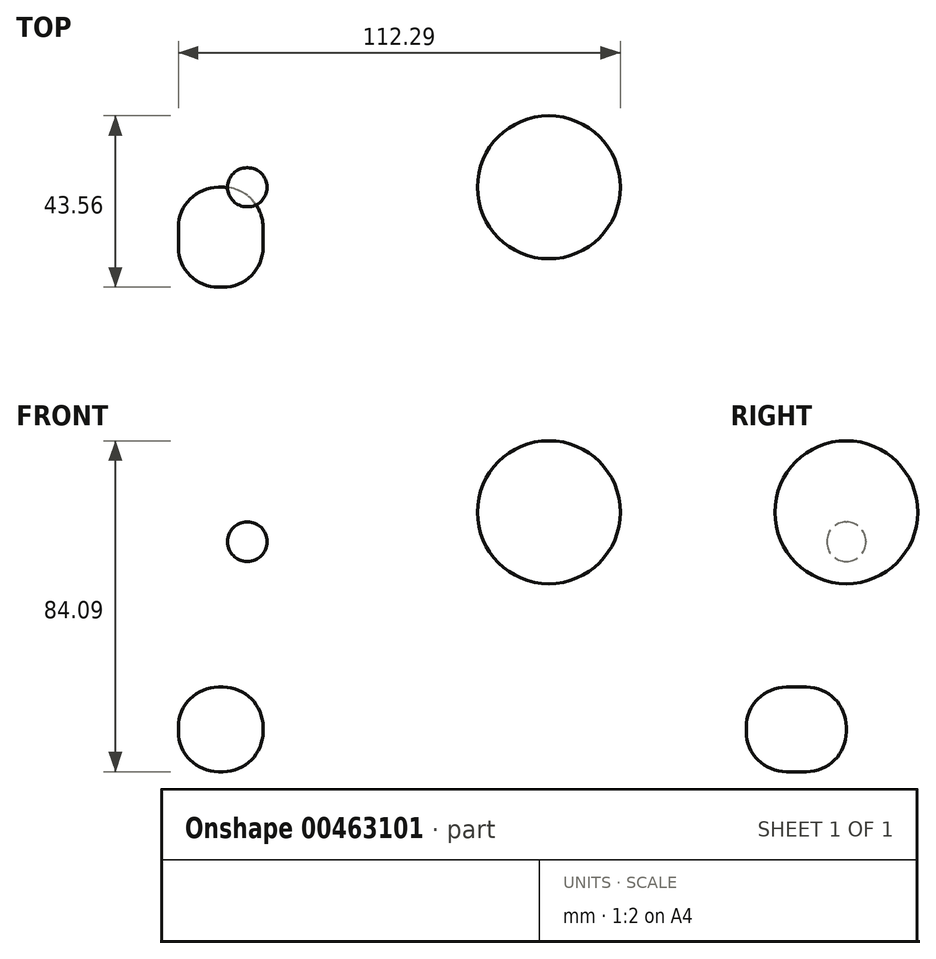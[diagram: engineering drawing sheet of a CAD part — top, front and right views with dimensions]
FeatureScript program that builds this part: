
annotation { "Feature Type Name" : "Feature", "Feature Type Description" : "" }
export const myFeature = defineFeature(function(context is Context, id is Id, definition is map)
    precondition{}
    {
        {
            var Q0;
            Q0=qCreatedBy(makeId("Top.planeOp"),FACE);
            var sketch = newSketch(context, id + "F0", { "sketchPlane" : qUnion([Q0])});
            skCircle(sketch, "E0", {"center": v(0, 0) * mm, "radius": 52.63 * mm});
            skSolve(sketch);
        }
        {
            var Q0;
            Q0=qCreatedBy(makeId("Front.planeOp"),FACE);
            var sketch = newSketch(context, id + "F1", { "sketchPlane" : qUnion([Q0])});
            skLineSegment(sketch, "E1.bottom", {"start": v(-124.76, -28.07) * mm, "end": v(-103.26, -28.07) * mm});
            skLineSegment(sketch, "E1.top", {"start": v(-124.76, -6.57) * mm, "end": v(-103.26, -6.57) * mm});
            skLineSegment(sketch, "E1.left", {"start": v(-124.76, -28.07) * mm, "end": v(-124.76, -6.57) * mm});
            skLineSegment(sketch, "E1.right", {"start": v(-103.26, -28.07) * mm, "end": v(-103.26, -6.57) * mm});
            skSolve(sketch);
        }
        {
            var Q0;
            Q0=makeQuery(id+"F1.imprint","IMPRINT",FACE,{"disambiguationData":[TD([[makeQuery(id+"F1.imprint","IMPRINT",EDGE,{"derivedFrom":sQuery(id+"F1.wireOp",EDGE,"E1.bottom")}),1.0]])]});
            extrude(context, id + "F2", {"entities" : qUnion([Q0]), "depth" : 25.4 * mm});
        }
        {
            var Q0;
            Q0=makeQuery(id+"F2.opExtrude","SWEPT_EDGE",EDGE,{"disambiguationData":[OSD([sQuery(id+"F1.wireOp",EDGE,"E1.bottom"),sQuery(id+"F1.wireOp",EDGE,"E1.right")])]});
            var Q1;
            Q1=makeQuery(id+"F2.opExtrude","CAP_EDGE",EDGE,{"disambiguationData":[OSD([sQuery(id+"F1.wireOp",EDGE,"E1.bottom")])],"isStart":false});
            var Q2;
            Q2=makeQuery(id+"F2.opExtrude","SWEPT_FACE",FACE,{"disambiguationData":[OSD([sQuery(id+"F1.wireOp",EDGE,"E1.bottom")])]});
            var Q3;
            Q3=makeQuery(id+"F2.opExtrude","CAP_FACE",FACE,{"disambiguationData":[OSD([sQuery(id+"F1.wireOp",EDGE,"E1.bottom"),sQuery(id+"F1.wireOp",EDGE,"E1.top"),sQuery(id+"F1.wireOp",EDGE,"E1.left"),sQuery(id+"F1.wireOp",EDGE,"E1.right")])],"isStart":false});
            var Q4;
            Q4=makeQuery(id+"F2.opExtrude","SWEPT_EDGE",EDGE,{"disambiguationData":[OSD([sQuery(id+"F1.wireOp",EDGE,"E1.top"),sQuery(id+"F1.wireOp",EDGE,"E1.left")])]});
            var Q5;
            Q5=makeQuery(id+"F2.opExtrude","SWEPT_FACE",FACE,{"disambiguationData":[OSD([sQuery(id+"F1.wireOp",EDGE,"E1.top")])]});
            var Q6;
            Q6=makeQuery(id+"F2.opExtrude","SWEPT_FACE",FACE,{"disambiguationData":[OSD([sQuery(id+"F1.wireOp",EDGE,"E1.left")])]});
            var Q7;
            Q7=makeQuery(id+"F2.opExtrude","CAP_EDGE",EDGE,{"disambiguationData":[OSD([sQuery(id+"F1.wireOp",EDGE,"E1.bottom")])],"isStart":true});
            var Q8;
            Q8=makeQuery(id+"F2.opExtrude","CAP_EDGE",EDGE,{"disambiguationData":[OSD([sQuery(id+"F1.wireOp",EDGE,"E1.top")])],"isStart":false});
            var Q9;
            Q9=makeQuery(id+"F2.opExtrude","CAP_FACE",FACE,{"disambiguationData":[OSD([sQuery(id+"F1.wireOp",EDGE,"E1.bottom"),sQuery(id+"F1.wireOp",EDGE,"E1.top"),sQuery(id+"F1.wireOp",EDGE,"E1.left"),sQuery(id+"F1.wireOp",EDGE,"E1.right")])],"isStart":true});
            var Q10;
            Q10=makeQuery(id+"F2.opExtrude","SWEPT_FACE",FACE,{"disambiguationData":[OSD([sQuery(id+"F1.wireOp",EDGE,"E1.right")])]});
            var Q11;
            Q11=makeQuery(id+"F2.opExtrude","SWEPT_EDGE",EDGE,{"disambiguationData":[OSD([sQuery(id+"F1.wireOp",EDGE,"E1.bottom"),sQuery(id+"F1.wireOp",EDGE,"E1.left")])]});
            var Q12;
            Q12=makeQuery(id+"F2.opExtrude","CAP_EDGE",EDGE,{"disambiguationData":[OSD([sQuery(id+"F1.wireOp",EDGE,"E1.left")])],"isStart":false});
            var Q13;
            Q13=makeQuery(id+"F2.opExtrude","CAP_EDGE",EDGE,{"disambiguationData":[OSD([sQuery(id+"F1.wireOp",EDGE,"E1.right")])],"isStart":true});
            var Q14;
            Q14=makeQuery(id+"F2.opExtrude","CAP_EDGE",EDGE,{"disambiguationData":[OSD([sQuery(id+"F1.wireOp",EDGE,"E1.left")])],"isStart":true});
            var Q15;
            Q15=makeQuery(id+"F2.opExtrude","CAP_EDGE",EDGE,{"disambiguationData":[OSD([sQuery(id+"F1.wireOp",EDGE,"E1.top")])],"isStart":true});
            var Q16;
            Q16=makeQuery(id+"F2.opExtrude","SWEPT_EDGE",EDGE,{"disambiguationData":[OSD([sQuery(id+"F1.wireOp",EDGE,"E1.top"),sQuery(id+"F1.wireOp",EDGE,"E1.right")])]});
            var Q17;
            Q17=makeQuery(id+"F2.opExtrude","CAP_EDGE",EDGE,{"disambiguationData":[OSD([sQuery(id+"F1.wireOp",EDGE,"E1.right")])],"isStart":false});
            fillet(context, id + "F3", {"entities" : qUnion([Q0, Q1, Q2, Q3, Q4, Q5, Q6, Q7, Q8, Q9, Q10, Q11, Q12, Q13, Q14, Q15, Q16, Q17]), "radius" : 10.16 * mm, "tangentPropagation" : true, "allowEdgeOverflow" : false});
        }
        {
            var Q0;
            Q0=qCreatedBy(makeId("Front.planeOp"),FACE);
            var sketch = newSketch(context, id + "F4", { "sketchPlane" : qUnion([Q0])});
            skLineSegment(sketch, "E2", {"start": v(-12.47, 37.85) * mm, "end": v(-48.8, 37.85) * mm});
            skArc(sketch, "E3", {"start": v(-48.8, 37.85) * mm, "mid": v(-30.64, 19.7) * mm, "end": v(-12.47, 37.85) * mm});
            skSolve(sketch);
        }
        {
            var Q0;
            Q0=makeQuery(id+"F4.imprint","IMPRINT",FACE,{"disambiguationData":[TD([[makeQuery(id+"F4.imprint","IMPRINT",EDGE,{"derivedFrom":sQuery(id+"F4.wireOp",EDGE,"E2")}),1.0]])]});
            var Q1;
            Q1=sQuery(id+"F4.wireOp",EDGE,"E2");
            revolve(context, id + "F5", {"entities" : qUnion([Q0]), "axis" : qUnion([Q1]), "revolveType" : RevolveType.FULL});
        }
        {
            var Q0;
            Q0=qCreatedBy(makeId("Front.planeOp"),FACE);
            var sketch = newSketch(context, id + "F6", { "sketchPlane" : qUnion([Q0])});
            skLineSegment(sketch, "E4.bottom", {"start": v(-102.24, 35.38) * mm, "end": v(-112.24, 35.38) * mm});
            skLineSegment(sketch, "E4.top", {"start": v(-102.24, 25.38) * mm, "end": v(-112.24, 25.38) * mm});
            skLineSegment(sketch, "E4.left", {"start": v(-102.24, 35.38) * mm, "end": v(-102.24, 25.38) * mm});
            skLineSegment(sketch, "E4.right", {"start": v(-112.24, 35.38) * mm, "end": v(-112.24, 25.38) * mm});
            skSolve(sketch);
        }
        {
            var Q0;
            Q0 = qSketchRegion(id + "F6", true);
            extrude(context, id + "F7", {"entities" : qUnion([Q0]), "endBound" : BoundingType.SYMMETRIC, "depth" : 9.9 * mm});
        }
        {
            var Q0;
            Q0=makeQuery(id+"F7.opExtrude","SWEPT_FACE",FACE,{"disambiguationData":[OSD([sQuery(id+"F6.wireOp",EDGE,"E4.right")])]});
            var Q1;
            Q1=makeQuery(id+"F7.opExtrude","SWEPT_FACE",FACE,{"disambiguationData":[OSD([sQuery(id+"F6.wireOp",EDGE,"E4.left")])]});
            var Q2;
            Q2=makeQuery(id+"F7.opExtrude","SWEPT_EDGE",EDGE,{"disambiguationData":[OSD([sQuery(id+"F6.wireOp",EDGE,"E4.top"),sQuery(id+"F6.wireOp",EDGE,"E4.right")])]});
            var Q3;
            Q3=makeQuery(id+"F7.opExtrude","CAP_FACE",FACE,{"disambiguationData":[OSD([sQuery(id+"F6.wireOp",EDGE,"E4.bottom"),sQuery(id+"F6.wireOp",EDGE,"E4.top"),sQuery(id+"F6.wireOp",EDGE,"E4.left"),sQuery(id+"F6.wireOp",EDGE,"E4.right")])],"isStart":true});
            var Q4;
            Q4=makeQuery(id+"F7.opExtrude","SWEPT_EDGE",EDGE,{"disambiguationData":[OSD([sQuery(id+"F6.wireOp",EDGE,"E4.bottom"),sQuery(id+"F6.wireOp",EDGE,"E4.right")])]});
            var Q5;
            Q5=makeQuery(id+"F7.opExtrude","SWEPT_FACE",FACE,{"disambiguationData":[OSD([sQuery(id+"F6.wireOp",EDGE,"E4.bottom")])]});
            var Q6;
            Q6=makeQuery(id+"F7.opExtrude","SWEPT_EDGE",EDGE,{"disambiguationData":[OSD([sQuery(id+"F6.wireOp",EDGE,"E4.bottom"),sQuery(id+"F6.wireOp",EDGE,"E4.left")])]});
            var Q7;
            Q7=makeQuery(id+"F7.opExtrude","CAP_EDGE",EDGE,{"disambiguationData":[OSD([sQuery(id+"F6.wireOp",EDGE,"E4.right")])],"isStart":false});
            var Q8;
            Q8=makeQuery(id+"F7.opExtrude","CAP_EDGE",EDGE,{"disambiguationData":[OSD([sQuery(id+"F6.wireOp",EDGE,"E4.right")])],"isStart":true});
            var Q9;
            Q9=makeQuery(id+"F7.opExtrude","CAP_EDGE",EDGE,{"disambiguationData":[OSD([sQuery(id+"F6.wireOp",EDGE,"E4.left")])],"isStart":false});
            var Q10;
            Q10=makeQuery(id+"F7.opExtrude","CAP_EDGE",EDGE,{"disambiguationData":[OSD([sQuery(id+"F6.wireOp",EDGE,"E4.left")])],"isStart":true});
            var Q11;
            Q11=makeQuery(id+"F7.opExtrude","CAP_EDGE",EDGE,{"disambiguationData":[OSD([sQuery(id+"F6.wireOp",EDGE,"E4.top")])],"isStart":false});
            var Q12;
            Q12=makeQuery(id+"F7.opExtrude","CAP_EDGE",EDGE,{"disambiguationData":[OSD([sQuery(id+"F6.wireOp",EDGE,"E4.top")])],"isStart":true});
            var Q13;
            Q13=makeQuery(id+"F7.opExtrude","CAP_EDGE",EDGE,{"disambiguationData":[OSD([sQuery(id+"F6.wireOp",EDGE,"E4.bottom")])],"isStart":false});
            var Q14;
            Q14=makeQuery(id+"F7.opExtrude","CAP_EDGE",EDGE,{"disambiguationData":[OSD([sQuery(id+"F6.wireOp",EDGE,"E4.bottom")])],"isStart":true});
            var Q15;
            Q15=makeQuery(id+"F7.opExtrude","SWEPT_FACE",FACE,{"disambiguationData":[OSD([sQuery(id+"F6.wireOp",EDGE,"E4.top")])]});
            var Q16;
            Q16=makeQuery(id+"F7.opExtrude","CAP_FACE",FACE,{"disambiguationData":[OSD([sQuery(id+"F6.wireOp",EDGE,"E4.bottom"),sQuery(id+"F6.wireOp",EDGE,"E4.top"),sQuery(id+"F6.wireOp",EDGE,"E4.left"),sQuery(id+"F6.wireOp",EDGE,"E4.right")])],"isStart":false});
            var Q17;
            Q17=makeQuery(id+"F7.opExtrude","SWEPT_EDGE",EDGE,{"disambiguationData":[OSD([sQuery(id+"F6.wireOp",EDGE,"E4.top"),sQuery(id+"F6.wireOp",EDGE,"E4.left")])]});
            fillet(context, id + "F8", {"entities" : qUnion([Q0, Q1, Q2, Q3, Q4, Q5, Q6, Q7, Q8, Q9, Q10, Q11, Q12, Q13, Q14, Q15, Q16, Q17]), "radius" : 4.9 * mm, "tangentPropagation" : true, "allowEdgeOverflow" : false});
        }
    });
